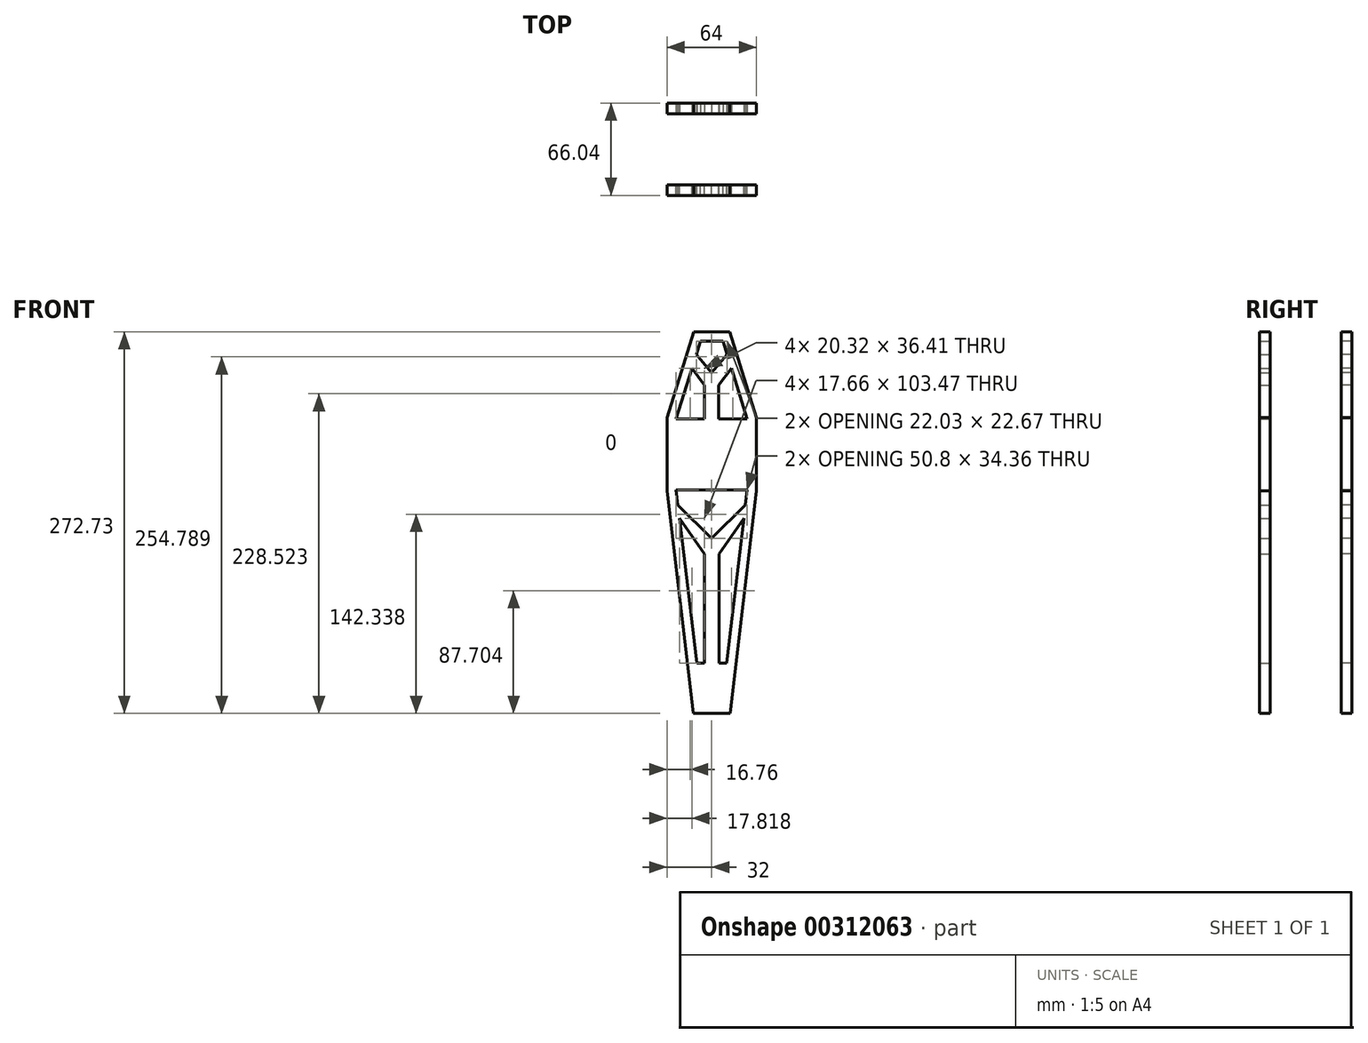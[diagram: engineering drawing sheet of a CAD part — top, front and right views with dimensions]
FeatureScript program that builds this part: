
annotation { "Feature Type Name" : "Feature", "Feature Type Description" : "" }
export const myFeature = defineFeature(function(context is Context, id is Id, definition is map)
    precondition{}
    {
        {
            var Q0;
            Q0=qCreatedBy(makeId("Front.planeOp"),FACE);
            var sketch = newSketch(context, id + "F0", { "sketchPlane" : qUnion([Q0])});
            skLineSegment(sketch, "E0.bottom", {"start": v(-25.4, 0) * mm, "end": v(25.4, 0) * mm});
            skLineSegment(sketch, "E0.top", {"start": v(-25.4, -50.8) * mm, "end": v(25.4, -50.8) * mm});
            skLineSegment(sketch, "E0.left", {"start": v(-25.4, 0) * mm, "end": v(-25.4, -50.8) * mm});
            skLineSegment(sketch, "E0.right", {"start": v(25.4, 0) * mm, "end": v(25.4, -50.8) * mm});
            skLineSegment(sketch, "E1", {"start": v(0, -25.4) * mm, "end": v(0, 55.8) * mm, "construction": true});
            skPoint(sketch, "E1.startSnap0", {"position": v(0, -50.8) * mm});
            skPoint(sketch, "E1.startSnap1", {"position": v(-25.4, -25.4) * mm});
            skPoint(sketch, "E1.endSnap0", {"position": v(0, 0) * mm});
            skLineSegment(sketch, "E2", {"start": v(0, 55.8) * mm, "end": v(-7.99, 55.8) * mm});
            skLineSegment(sketch, "E3", {"start": v(-7.99, 55.8) * mm, "end": v(0, 55.8) * mm});
            skLineSegment(sketch, "E4", {"start": v(7.99, 55.8) * mm, "end": v(0, 55.8) * mm});
            skLineSegment(sketch, "E5", {"start": v(-25.4, 0) * mm, "end": v(-7.99, 55.8) * mm});
            skLineSegment(sketch, "E6", {"start": v(25.4, 0) * mm, "end": v(7.99, 55.8) * mm});
            skLineSegment(sketch, "E7", {"start": v(0, -25.4) * mm, "end": v(0, -174.35) * mm, "construction": true});
            skLineSegment(sketch, "E8", {"start": v(0, -174.35) * mm, "end": v(-10.7, -174.35) * mm});
            skLineSegment(sketch, "E9", {"start": v(0, -174.35) * mm, "end": v(10.7, -174.35) * mm});
            skLineSegment(sketch, "E10", {"start": v(-10.7, -174.35) * mm, "end": v(-25.4, -50.8) * mm});
            skLineSegment(sketch, "E11", {"start": v(10.7, -174.35) * mm, "end": v(25.4, -50.8) * mm});
            skLineSegment(sketch, "E12", {"start": v(-5.08, 0) * mm, "end": v(-5.08, 24.34) * mm});
            skLineSegment(sketch, "E13", {"start": v(5.08, 0) * mm, "end": v(5.08, 24.34) * mm});
            skLineSegment(sketch, "E14", {"start": v(11.01, 46.1) * mm, "end": v(0, 33.14) * mm});
            skLineSegment(sketch, "E15", {"start": v(14.04, 36.4) * mm, "end": v(5.08, 24.34) * mm});
            skLineSegment(sketch, "E16", {"start": v(-14.04, 36.4) * mm, "end": v(-5.08, 24.34) * mm});
            skLineSegment(sketch, "E17", {"start": v(-11.01, 46.1) * mm, "end": v(0, 33.14) * mm});
            skLineSegment(sketch, "E18", {"start": v(0, 33.14) * mm, "end": v(-5.08, 24.34) * mm});
            skLineSegment(sketch, "E19", {"start": v(0, 33.14) * mm, "end": v(5.08, 24.34) * mm});
            skLineSegment(sketch, "E20", {"start": v(-5.08, 24.34) * mm, "end": v(5.08, 24.34) * mm});
            skLineSegment(sketch, "E21", {"start": v(-24.15, -61.34) * mm, "end": v(0, -85.16) * mm});
            skLineSegment(sketch, "E22", {"start": v(-23.01, -70.88) * mm, "end": v(-5.35, -96.3) * mm});
            skLineSegment(sketch, "E23", {"start": v(24.15, -61.34) * mm, "end": v(0, -85.16) * mm});
            skLineSegment(sketch, "E24", {"start": v(23.01, -70.88) * mm, "end": v(5.35, -96.3) * mm});
            skLineSegment(sketch, "E25", {"start": v(-5.35, -174.35) * mm, "end": v(-5.35, -96.3) * mm});
            skLineSegment(sketch, "E26", {"start": v(5.35, -174.35) * mm, "end": v(5.35, -96.3) * mm});
            skLineSegment(sketch, "E27", {"start": v(-5.35, -96.3) * mm, "end": v(0, -85.16) * mm});
            skLineSegment(sketch, "E28", {"start": v(0, -85.16) * mm, "end": v(5.35, -96.3) * mm});
            skLineSegment(sketch, "E29", {"start": v(-5.35, -96.3) * mm, "end": v(5.35, -96.3) * mm});
            skLineSegment(sketch, "E30.0", {"start": v(-32, 1) * mm, "end": v(-32, -51.2) * mm});
            skLineSegment(sketch, "E30.1", {"start": v(-16.57, -180.96) * mm, "end": v(-32, -51.2) * mm});
            skLineSegment(sketch, "E30.2", {"start": v(-32, 1) * mm, "end": v(-12.85, 62.4) * mm});
            skLineSegment(sketch, "E30.3", {"start": v(0, -180.96) * mm, "end": v(-16.57, -180.96) * mm});
            skLineSegment(sketch, "E30.4", {"start": v(0, -180.96) * mm, "end": v(16.57, -180.96) * mm});
            skLineSegment(sketch, "E30.5", {"start": v(16.57, -180.96) * mm, "end": v(32, -51.2) * mm});
            skLineSegment(sketch, "E30.6", {"start": v(-12.85, 62.4) * mm, "end": v(0, 62.4) * mm});
            skLineSegment(sketch, "E30.7", {"start": v(12.85, 62.4) * mm, "end": v(0, 62.4) * mm});
            skLineSegment(sketch, "E30.8", {"start": v(32, 1) * mm, "end": v(12.85, 62.4) * mm});
            skLineSegment(sketch, "E30.9", {"start": v(32, 1) * mm, "end": v(32, -51.2) * mm});
            skLineSegment(sketch, "E31", {"start": v(-16.57, -180.96) * mm, "end": v(-13.08, -210.32) * mm});
            skLineSegment(sketch, "E32", {"start": v(16.57, -180.96) * mm, "end": v(13.08, -210.32) * mm});
            skLineSegment(sketch, "E33", {"start": v(-13.08, -210.32) * mm, "end": v(13.08, -210.32) * mm});
            skSolve(sketch);
        }
        {
            var Q0;
            Q0=qCreatedBy(makeId("Front.planeOp"),FACE);
            cPlane(context, id + "F1", {"entities" : qUnion([Q0]), "cplaneType" : CPlaneType.OFFSET, "offset" : 25.4 * mm, "oppositeDirection" : true, "width" : 152.4 * mm, "height" : 152.4 * mm});
        }
        {
            var Q0;
            Q0=makeQuery(id+"F0.imprint","IMPRINT",FACE,{"disambiguationData":[TD([[makeQuery(id+"F0.imprint","IMPRINT",EDGE,{"derivedFrom":sQuery(id+"F0.wireOp",EDGE,"E18")}),1.0]])]});
            var Q1;
            {var subQ0=sQuery(id+"F0.wireOp",EDGE,"E12");Q1=makeQuery(id+"F0.imprint","IMPRINT",FACE,{"disambiguationData":[TD([[makeQuery(id+"F0.imprint","IMPRINT",EDGE,{"derivedFrom":subQ0}),-1.0]])]});}
            var Q2;
            {var subQ0=sQuery(id+"F0.wireOp",EDGE,"E14");Q2=makeQuery(id+"F0.imprint","IMPRINT",FACE,{"disambiguationData":[TD([[makeQuery(id+"F0.imprint","IMPRINT",EDGE,{"derivedFrom":subQ0}),1.0]])]});}
            var Q3;
            {var subQ0=sQuery(id+"F0.wireOp",EDGE,"E16");Q3=makeQuery(id+"F0.imprint","IMPRINT",FACE,{"disambiguationData":[TD([[makeQuery(id+"F0.imprint","IMPRINT",EDGE,{"derivedFrom":subQ0}),1.0]])]});}
            var Q4;
            {var subQ8=sQuery(id+"F0.wireOp",EDGE,"E0.left");Q4=makeQuery(id+"F0.imprint","IMPRINT",FACE,{"disambiguationData":[TD([[makeQuery(id+"F0.imprint","IMPRINT",EDGE,{"derivedFrom":subQ8}),-1.0]])]});}
            var Q5;
            Q5=makeQuery(id+"F0.imprint","IMPRINT",FACE,{"disambiguationData":[TD([[makeQuery(id+"F0.imprint","IMPRINT",EDGE,{"derivedFrom":sQuery(id+"F0.wireOp",EDGE,"E0.top")}),1.0]])]});
            var Q6;
            {var subQ0=sQuery(id+"F0.wireOp",EDGE,"E21");Q6=makeQuery(id+"F0.imprint","IMPRINT",FACE,{"disambiguationData":[TD([[makeQuery(id+"F0.imprint","IMPRINT",EDGE,{"derivedFrom":subQ0}),-1.0]])]});}
            var Q7;
            {var subQ0=sQuery(id+"F0.wireOp",EDGE,"E23");Q7=makeQuery(id+"F0.imprint","IMPRINT",FACE,{"disambiguationData":[TD([[makeQuery(id+"F0.imprint","IMPRINT",EDGE,{"derivedFrom":subQ0}),1.0]])]});}
            var Q8;
            Q8=makeQuery(id+"F0.imprint","IMPRINT",FACE,{"disambiguationData":[TD([[makeQuery(id+"F0.imprint","IMPRINT",EDGE,{"derivedFrom":sQuery(id+"F0.wireOp",EDGE,"E27")}),-1.0]])]});
            var Q9;
            {var subQ4=sQuery(id+"F0.wireOp",EDGE,"E25");Q9=makeQuery(id+"F0.imprint","IMPRINT",FACE,{"disambiguationData":[TD([[makeQuery(id+"F0.imprint","IMPRINT",EDGE,{"derivedFrom":subQ4}),-1.0]])]});}
            extrude(context, id + "F2", {"entities" : qUnion([Q0, Q1, Q2, Q3, Q4, Q5, Q6, Q7, Q8, Q9]), "depth" : 7.62 * mm});
        }
        {
            var Q0;
            Q0=makeQuery(id+"F0.imprint","IMPRINT",FACE,{"disambiguationData":[TD([[makeQuery(id+"F0.imprint","IMPRINT",EDGE,{"derivedFrom":sQuery(id+"F0.wireOp",EDGE,"E30.3")}),1.0]])]});
            extrude(context, id + "F3", {"entities" : qUnion([Q0]), "operationType" : NewBodyOperationType.ADD, "depth" : 7.62 * mm});
        }
        {
            var Q0;
            Q0=makeQuery(id+"F2.opExtrude","SWEPT_BODY",BODY,{"disambiguationData":[OSD([sQuery(id+"F0.wireOp",EDGE,"E0.bottom"),sQuery(id+"F0.wireOp",EDGE,"E0.top"),sQuery(id+"F0.wireOp",EDGE,"E3"),sQuery(id+"F0.wireOp",EDGE,"E4"),sQuery(id+"F0.wireOp",EDGE,"E5"),sQuery(id+"F0.wireOp",EDGE,"E6"),sQuery(id+"F0.wireOp",EDGE,"E8"),sQuery(id+"F0.wireOp",EDGE,"E9"),sQuery(id+"F0.wireOp",EDGE,"E10"),sQuery(id+"F0.wireOp",EDGE,"E11"),sQuery(id+"F0.wireOp",EDGE,"E12"),sQuery(id+"F0.wireOp",EDGE,"E13"),sQuery(id+"F0.wireOp",EDGE,"E14"),sQuery(id+"F0.wireOp",EDGE,"E15"),sQuery(id+"F0.wireOp",EDGE,"E16"),sQuery(id+"F0.wireOp",EDGE,"E17"),sQuery(id+"F0.wireOp",EDGE,"E21"),sQuery(id+"F0.wireOp",EDGE,"E22"),sQuery(id+"F0.wireOp",EDGE,"E23"),sQuery(id+"F0.wireOp",EDGE,"E24"),sQuery(id+"F0.wireOp",EDGE,"E25"),sQuery(id+"F0.wireOp",EDGE,"E26"),sQuery(id+"F0.wireOp",EDGE,"E30.0"),sQuery(id+"F0.wireOp",EDGE,"E30.1"),sQuery(id+"F0.wireOp",EDGE,"E30.2"),sQuery(id+"F0.wireOp",EDGE,"E30.3"),sQuery(id+"F0.wireOp",EDGE,"E30.4"),sQuery(id+"F0.wireOp",EDGE,"E30.5"),sQuery(id+"F0.wireOp",EDGE,"E30.6"),sQuery(id+"F0.wireOp",EDGE,"E30.7"),sQuery(id+"F0.wireOp",EDGE,"E30.8"),sQuery(id+"F0.wireOp",EDGE,"E30.9")])]});
            var Q1;
            Q1=qCreatedBy(id+"F1.planeOp",FACE);
            mirror(context, id + "F4", {"entities" : qUnion([Q0]), "mirrorPlane" : qUnion([Q1])});
        }
    });
